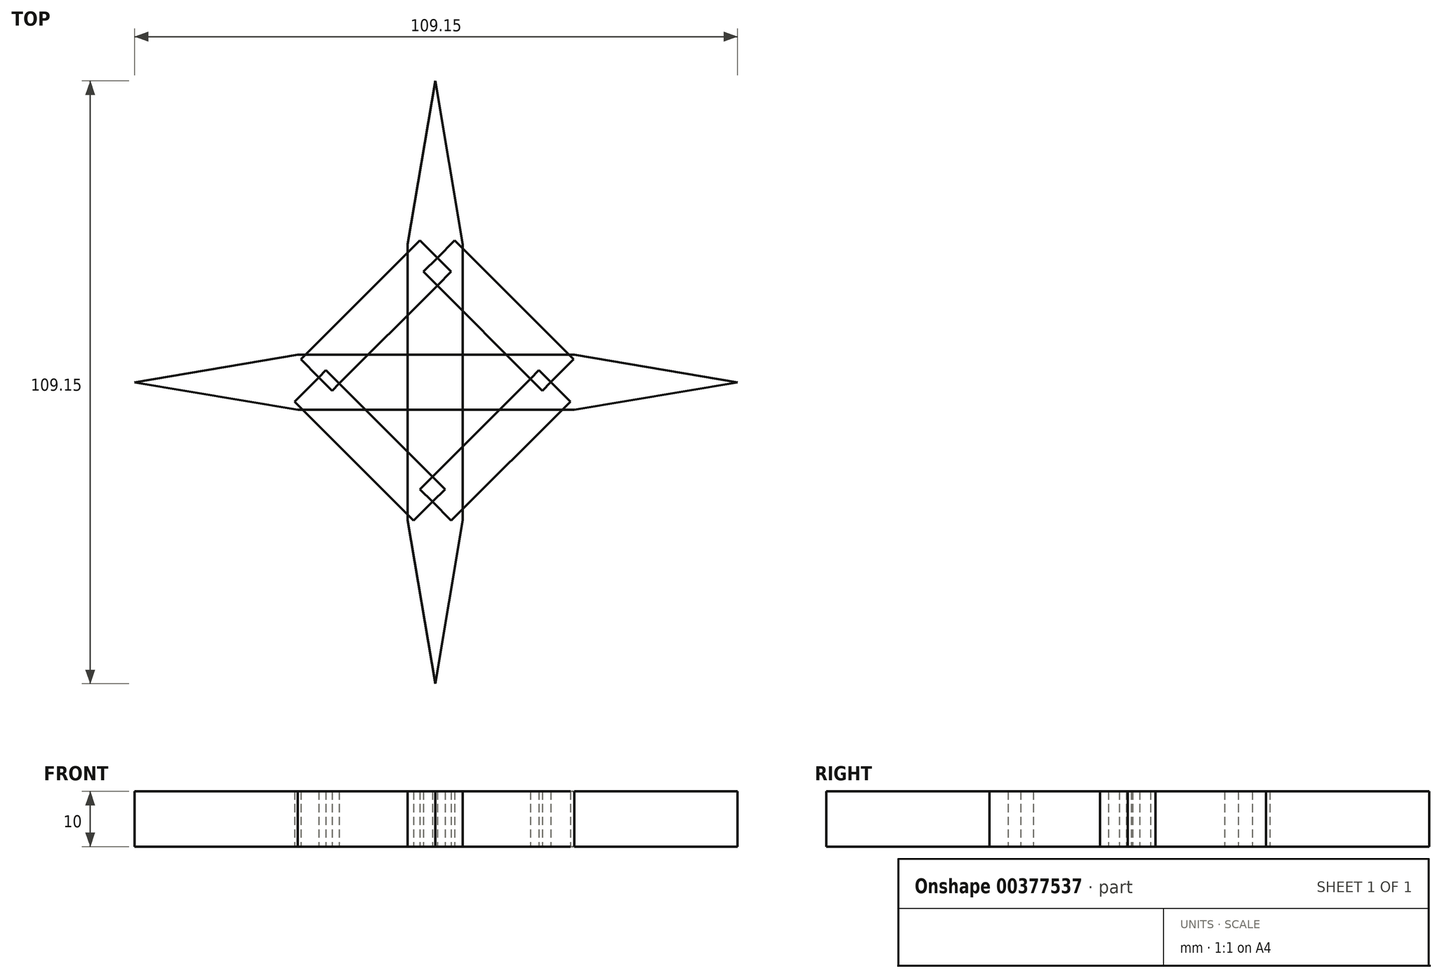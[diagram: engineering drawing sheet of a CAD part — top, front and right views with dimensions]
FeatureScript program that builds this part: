
annotation { "Feature Type Name" : "Feature", "Feature Type Description" : "" }
export const myFeature = defineFeature(function(context is Context, id is Id, definition is map)
    precondition{}
    {
        {
            var Q0;
            Q0=qCreatedBy(makeId("Top.planeOp"),FACE);
            var sketch = newSketch(context, id + "F0", { "sketchPlane" : qUnion([Q0])});
            skLineSegment(sketch, "E0.bottom", {"start": v(-5, 25) * mm, "end": v(5, 25) * mm});
            skLineSegment(sketch, "E0.top", {"start": v(-5, -25) * mm, "end": v(5, -25) * mm});
            skLineSegment(sketch, "E0.left", {"start": v(-5, 25) * mm, "end": v(-5, -25) * mm});
            skLineSegment(sketch, "E0.right", {"start": v(5, 25) * mm, "end": v(5, -25) * mm});
            skPoint(sketch, "E0.middle", {"position": v(0, 0) * mm});
            skLineSegment(sketch, "E1", {"start": v(-5, 25) * mm, "end": v(0, 54.58) * mm});
            skLineSegment(sketch, "E2", {"start": v(0, 54.58) * mm, "end": v(5, 25) * mm});
            skLineSegment(sketch, "E3", {"start": v(-5, -25) * mm, "end": v(0, -54.57) * mm});
            skLineSegment(sketch, "E4", {"start": v(0, -54.57) * mm, "end": v(5, -25) * mm});
            skSolve(sketch);
        }
        {
            var Q0;
            Q0=qCreatedBy(makeId("Top.planeOp"),FACE);
            var sketch = newSketch(context, id + "F1", { "sketchPlane" : qUnion([Q0])});
            skLineSegment(sketch, "E5.bottom", {"start": v(25.15, 5) * mm, "end": v(25.15, -5) * mm});
            skLineSegment(sketch, "E5.top", {"start": v(-24.85, 5) * mm, "end": v(-24.85, -5) * mm});
            skLineSegment(sketch, "E5.left", {"start": v(25.15, 5) * mm, "end": v(-24.85, 5) * mm});
            skLineSegment(sketch, "E5.right", {"start": v(25.15, -5) * mm, "end": v(-24.85, -5) * mm});
            skLineSegment(sketch, "E6", {"start": v(25.15, 5) * mm, "end": v(54.73, 0) * mm});
            skLineSegment(sketch, "E7", {"start": v(54.73, 0) * mm, "end": v(25.15, -5) * mm});
            skLineSegment(sketch, "E8", {"start": v(-24.85, 5) * mm, "end": v(-54.42, 0) * mm});
            skLineSegment(sketch, "E9", {"start": v(-54.42, 0) * mm, "end": v(-24.85, -5) * mm});
            skSolve(sketch);
        }
        {
            var Q0;
            Q0=qCreatedBy(makeId("Top.planeOp"),FACE);
            var sketch = newSketch(context, id + "F2", { "sketchPlane" : qUnion([Q0])});
            skLineSegment(sketch, "E10.bottom", {"start": v(2.9, 20.03) * mm, "end": v(-18.65, -1.52) * mm});
            skLineSegment(sketch, "E10.top", {"start": v(-2.77, 25.7) * mm, "end": v(-24.33, 4.15) * mm});
            skLineSegment(sketch, "E10.left", {"start": v(2.9, 20.03) * mm, "end": v(-2.77, 25.7) * mm});
            skLineSegment(sketch, "E10.right", {"start": v(-18.65, -1.52) * mm, "end": v(-24.33, 4.15) * mm});
            skPoint(sketch, "E10.middle", {"position": v(-10.71, 12.09) * mm});
            skLineSegment(sketch, "E11.bottom", {"start": v(3.53, 25.7) * mm, "end": v(25.08, 4.15) * mm});
            skLineSegment(sketch, "E11.top", {"start": v(-2.15, 20.03) * mm, "end": v(19.4, -1.52) * mm});
            skLineSegment(sketch, "E11.left", {"start": v(3.53, 25.7) * mm, "end": v(-2.15, 20.03) * mm});
            skLineSegment(sketch, "E11.right", {"start": v(25.08, 4.15) * mm, "end": v(19.4, -1.52) * mm});
            skPoint(sketch, "E11.middle", {"position": v(11.47, 12.09) * mm});
            skLineSegment(sketch, "E12.bottom", {"start": v(-19.77, 2.19) * mm, "end": v(1.78, -19.37) * mm});
            skLineSegment(sketch, "E12.top", {"start": v(-25.45, -3.49) * mm, "end": v(-3.9, -25.04) * mm});
            skLineSegment(sketch, "E12.left", {"start": v(-19.77, 2.19) * mm, "end": v(-25.45, -3.49) * mm});
            skLineSegment(sketch, "E12.right", {"start": v(1.78, -19.37) * mm, "end": v(-3.9, -25.04) * mm});
            skPoint(sketch, "E12.middle", {"position": v(-11.83, -11.43) * mm});
            skLineSegment(sketch, "E13.bottom", {"start": v(24.45, -3.49) * mm, "end": v(2.9, -25.04) * mm});
            skLineSegment(sketch, "E13.top", {"start": v(18.78, 2.19) * mm, "end": v(-2.77, -19.37) * mm});
            skLineSegment(sketch, "E13.left", {"start": v(24.45, -3.49) * mm, "end": v(18.78, 2.19) * mm});
            skLineSegment(sketch, "E13.right", {"start": v(2.9, -25.04) * mm, "end": v(-2.77, -19.37) * mm});
            skPoint(sketch, "E13.middle", {"position": v(10.84, -11.43) * mm});
            skSolve(sketch);
        }
        {
            var Q0;
            {var subQ1=sQuery(id+"F2.wireOp",EDGE,"E10.top");Q0=makeQuery(id+"F2.imprint","IMPRINT",FACE,{"disambiguationData":[TD([[makeQuery(id+"F2.imprint","IMPRINT",EDGE,{"derivedFrom":subQ1}),1.0]])]});}
            var Q1;
            Q1=makeQuery(id+"F0.imprint","IMPRINT",FACE,{"disambiguationData":[TD([[makeQuery(id+"F0.imprint","IMPRINT",EDGE,{"derivedFrom":sQuery(id+"F0.wireOp",EDGE,"E0.bottom")}),-1.0]])]});
            var Q2;
            {var subQ0=sQuery(id+"F2.wireOp",EDGE,"E11.bottom");Q2=makeQuery(id+"F2.imprint","IMPRINT",FACE,{"disambiguationData":[TD([[makeQuery(id+"F2.imprint","IMPRINT",EDGE,{"derivedFrom":subQ0}),-1.0]])]});}
            var Q3;
            Q3=makeQuery(id+"F0.imprint","IMPRINT",FACE,{"disambiguationData":[TD([[makeQuery(id+"F0.imprint","IMPRINT",EDGE,{"derivedFrom":sQuery(id+"F0.wireOp",EDGE,"E0.bottom")}),1.0]])]});
            var Q4;
            Q4=makeQuery(id+"F1.imprint","IMPRINT",FACE,{"disambiguationData":[TD([[makeQuery(id+"F1.imprint","IMPRINT",EDGE,{"derivedFrom":sQuery(id+"F1.wireOp",EDGE,"E5.bottom")}),1.0]])]});
            var Q5;
            {var subQ13=sQuery(id+"F2.wireOp",EDGE,"E13.bottom");Q5=makeQuery(id+"F2.imprint","IMPRINT",FACE,{"disambiguationData":[TD([[makeQuery(id+"F2.imprint","IMPRINT",EDGE,{"derivedFrom":subQ13}),-1.0]])]});}
            var Q6;
            {var subQ0=sQuery(id+"F2.wireOp",EDGE,"E12.top");Q6=makeQuery(id+"F2.imprint","IMPRINT",FACE,{"disambiguationData":[TD([[makeQuery(id+"F2.imprint","IMPRINT",EDGE,{"derivedFrom":subQ0}),1.0]])]});}
            var Q7;
            Q7=makeQuery(id+"F1.imprint","IMPRINT",FACE,{"disambiguationData":[TD([[makeQuery(id+"F1.imprint","IMPRINT",EDGE,{"derivedFrom":sQuery(id+"F1.wireOp",EDGE,"E5.bottom")}),-1.0]])]});
            var Q8;
            Q8=makeQuery(id+"F1.imprint","IMPRINT",FACE,{"disambiguationData":[TD([[makeQuery(id+"F1.imprint","IMPRINT",EDGE,{"derivedFrom":sQuery(id+"F1.wireOp",EDGE,"E5.top")}),-1.0]])]});
            var Q9;
            Q9=makeQuery(id+"F0.imprint","IMPRINT",FACE,{"disambiguationData":[TD([[makeQuery(id+"F0.imprint","IMPRINT",EDGE,{"derivedFrom":sQuery(id+"F0.wireOp",EDGE,"E0.top")}),-1.0]])]});
            extrude(context, id + "F3", {"entities" : qUnion([Q0, Q1, Q2, Q3, Q4, Q5, Q6, Q7, Q8, Q9]), "depth" : 10 * mm});
        }
    });
